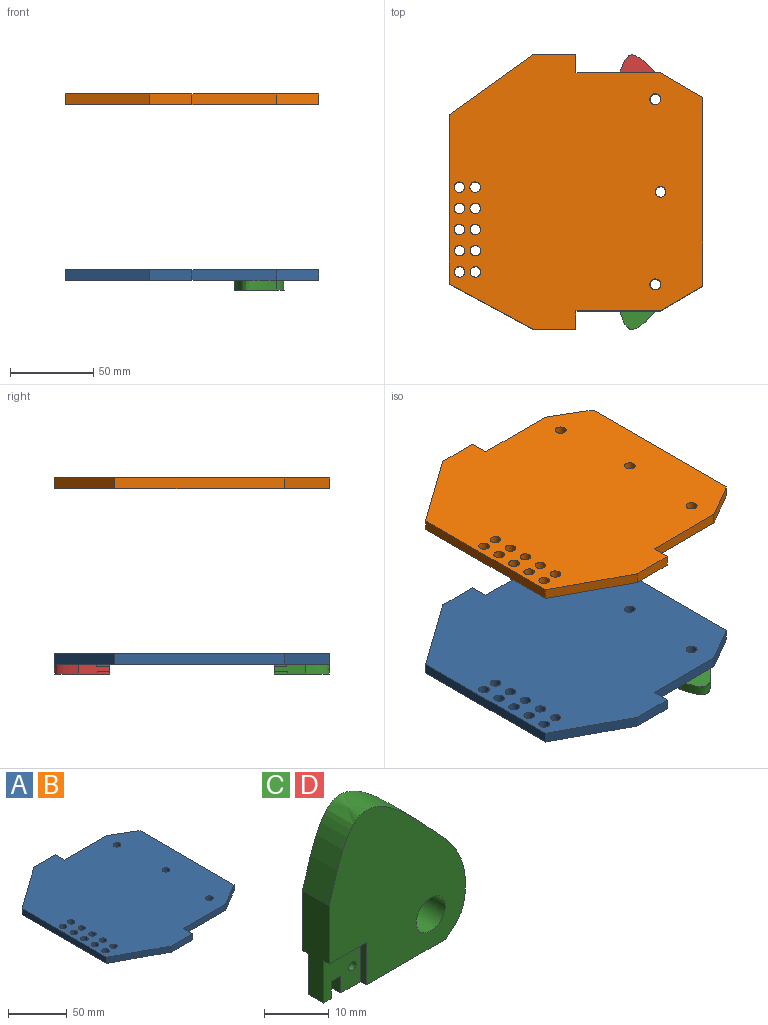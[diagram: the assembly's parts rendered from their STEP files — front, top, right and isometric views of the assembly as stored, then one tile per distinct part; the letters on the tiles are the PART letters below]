
ASSEMBLY  parts=4 mates=3
PART A: 27 faces, bbox 152.4x165.1x6.4 mm
  f0: plane 11.11x6.35mm, normal (1,0,0), area 70.6mm2, adj f1,f23,f25,f26
  f1: plane 50.8x6.35mm, normal (0,-1,0), area 322.6mm2, adj f0,f2,f25,f26
  f2: plane 25.4x14.85mm, normal (0.5,-0.86,0), area 186.8mm2, adj f1,f3,f25,f26
  f3: plane 113.17x6.35mm, normal (1,0,0), area 718.6mm2, adj f2,f4,f25,f26
  f4: plane 25.4x14.85mm, normal (0.5,0.86,0), area 186.8mm2, adj f3,f5,f25,f26
  f5: plane 50.8x6.35mm, normal (0,1,0), area 322.6mm2, adj f4,f6,f25,f26
  f6: plane 11.11x6.35mm, normal (1,0,0), area 70.6mm2, adj f5,f7,f25,f26
  f7: plane 25.4x6.35mm, normal (0,1,0), area 161.3mm2, adj f6,f8,f25,f26
  f8: plane 50.8x36.28mm, normal (-0.58,0.81,0), area 396.4mm2, adj f7,f9,f25,f26
  f9: plane 101.6x6.35mm, normal (-1,0,0), area 645.2mm2, adj f8,f10,f25,f26
  f10: plane 50.8x27.22mm, normal (-0.47,-0.88,0), area 366mm2, adj f9,f23,f25,f26
  f11: cylinder r=3.17mm len=6.35mm, axis (0,0,-1), area 126.7mm2, adj f25,f26
  f12: cylinder r=3.3mm len=6.6mm, axis (0,0,-1), area 131.7mm2, adj f25,f26
  f13: cylinder r=3.17mm len=6.35mm, axis (0,0,-1), area 126.7mm2, adj f25,f26
  f14: cylinder r=3.17mm len=6.35mm, axis (0,0,-1), area 126.7mm2, adj f25,f26
  f15: cylinder r=3.17mm len=6.35mm, axis (0,0,-1), area 126.7mm2, adj f25,f26
  f16: cylinder r=3.17mm len=6.35mm, axis (0,0,-1), area 126.7mm2, adj f25,f26
  f17: cylinder r=3.17mm len=6.35mm, axis (0,0,-1), area 126.7mm2, adj f25,f26
  f18: cylinder r=3.17mm len=6.35mm, axis (0,0,-1), area 126.7mm2, adj f25,f26
  f19: cylinder r=3.17mm len=6.35mm, axis (0,0,-1), area 126.7mm2, adj f25,f26
  f20: cylinder r=3.17mm len=6.35mm, axis (0,0,-1), area 126.7mm2, adj f25,f26
  f21: cylinder r=3.17mm len=6.35mm, axis (0,0,-1), area 126.7mm2, adj f25,f26
  f22: cylinder r=3.17mm len=6.35mm, axis (0,0,-1), area 126.7mm2, adj f25,f26
  f23: plane 25.4x6.35mm, normal (0,-1,0), area 161.3mm2, adj f0,f10,f25,f26
  f24: cylinder r=3.3mm len=6.6mm, axis (0,0,-1), area 131.7mm2, adj f25,f26
  f25: plane 165.1x152.4mm, normal (0,0,1), area 21060.7mm2, adj f0,f1,f2,f3,f4,f5,f6,f7
  f26: plane 165.1x152.4mm, normal (0,0,-1), area 21060.7mm2, adj f0,f1,f2,f3,f4,f5,f6,f7
PART B: same geometry as A
PART C: 18 faces, bbox 30.3x5.8x34 mm
  f0: plane 21.59x5.84mm, normal (0,0,-1), area 115.9mm2, adj f3,f6,f7,f11,f13,f14,f16,f17
  f1: plane 3.3x3.21mm, normal (1,0,0), area 10.6mm2, adj f2,f5,f14,f17
  f2: plane 3.3x2.08mm, normal (0,0,-1), area 6.9mm2, adj f1,f3,f14,f17
  f3: plane 3.3x3.21mm, normal (-1,0,0), area 10.6mm2, adj f0,f2,f14,f17
  f4: cylinder r=0.79mm len=3.3mm, axis (0,1,0), area 16.5mm2, adj f14,f17
  f5: plane 3.3x1.74mm, normal (0,0,-1), area 5.7mm2, adj f1,f9,f14,f17
  f6: plane 34.02x30.28mm, normal (0,-1,0), area 672.1mm2, adj f0,f7,f8,f9,f10,f12,f13
  f7: extruded ~19.05x5.84mm, area 127.6mm2, adj f0,f6,f8,f11
  f8: extruded ~25.4x14.07mm, area 232.8mm2, adj f6,f7,f9,f11
  f9: plane 19.05x5.84mm, normal (-1,0,0), area 91.4mm2, adj f5,f6,f8,f11,f12,f14,f15,f17
  f10: cylinder r=3.17mm len=6.35mm, axis (0,1,0), area 116.5mm2, adj f6,f11
  f11: plane 34.02x30.28mm, normal (0,1,0), area 679.1mm2, adj f0,f7,f8,f9,f10,f15,f16
  f12: plane 8.11x1.27mm, normal (0,0,-1), area 10.3mm2, adj f6,f9,f13,f14
  f13: plane 8.03x1.27mm, normal (-1,0,0), area 10.2mm2, adj f0,f6,f12,f14
  f14: plane 8.11x8.03mm, normal (0,-1,0), area 56.4mm2, adj f0,f1,f2,f3,f4,f5,f9,f12
  f15: plane 7.58x1.27mm, normal (0,0,-1), area 9.6mm2, adj f9,f11,f16,f17
  f16: plane 7.66x1.27mm, normal (-1,0,0), area 9.7mm2, adj f0,f11,f15,f17
  f17: plane 7.66x7.58mm, normal (0,1,0), area 49.4mm2, adj f0,f1,f2,f3,f4,f5,f9,f15
PART D: same geometry as C
PLACE A t=(-130.49,-112.91,11.24)mm
PLACE B t=(-130.49,-112.91,116.72)mm
PLACE C rot(axis=(1,0,0),90deg) t=(-87.24,-178.71,11.24)mm
PLACE D rot(axis=(-1,0,0),90deg) t=(-87.24,-47.11,5.4)mm
MATE cylindrical D.f10 <-> A.f12  axis (0,0,1) through (-108.26,-57.35,11.24)mm
MATE cylindrical C.f10 <-> A.f24  axis (0,0,1) through (-108.26,-168.47,11.24)mm
MATE cylindrical A.f12 <-> B.f12  axis (0,0,-1) through (-108.26,-57.35,11.24)mm
